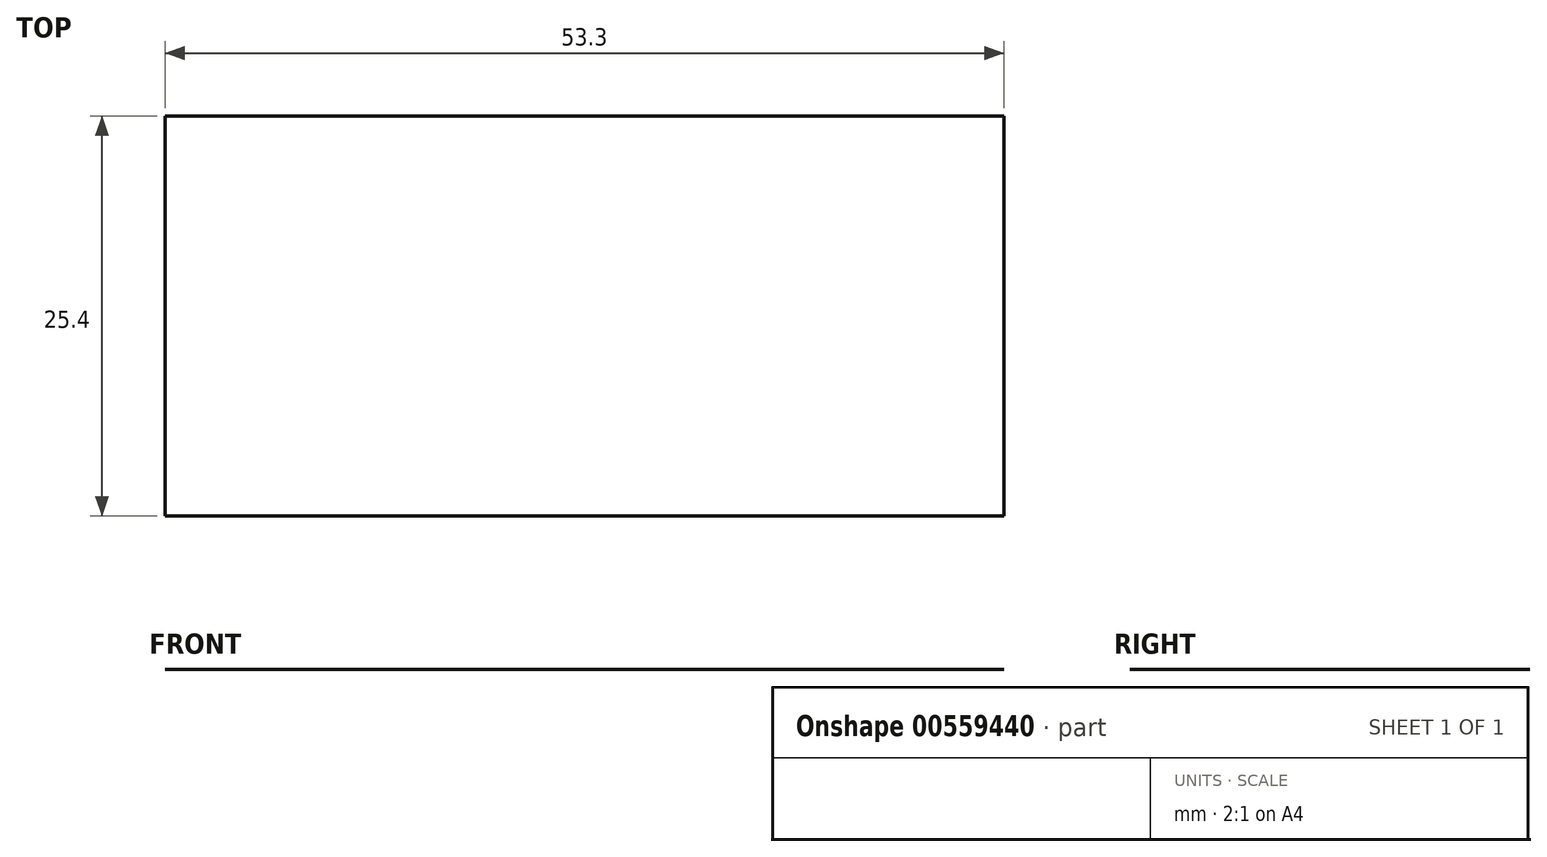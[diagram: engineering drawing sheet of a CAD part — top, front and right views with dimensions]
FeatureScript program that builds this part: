
annotation { "Feature Type Name" : "Feature", "Feature Type Description" : "" }
export const myFeature = defineFeature(function(context is Context, id is Id, definition is map)
    precondition{}
    {
        {
            var Q0;
            Q0=qCreatedBy(makeId("Front.planeOp"),FACE);
            var sketch = newSketch(context, id + "F0", { "sketchPlane" : qUnion([Q0])});
            skLineSegment(sketch, "E0.bottom", {"start": v(53.3, 0) * mm, "end": v(0, 0) * mm});
            skLineSegment(sketch, "E0.top", {"start": v(53.3, 31.95) * mm, "end": v(0, 31.95) * mm});
            skLineSegment(sketch, "E0.left", {"start": v(53.3, 0) * mm, "end": v(53.3, 31.95) * mm});
            skLineSegment(sketch, "E0.right", {"start": v(0, 0) * mm, "end": v(0, 31.95) * mm});
            skSolve(sketch);
        }
        {
            var Q0;
            Q0=sQuery(id+"F0.wireOp",EDGE,"E0.bottom");
            extrude(context, id + "F1", {"bodyType" : ToolBodyType.SURFACE, "surfaceEntities" : qUnion([Q0]), "depth" : 25.4 * mm, "offsetDistance" : 25.4 * mm});
        }
    });
